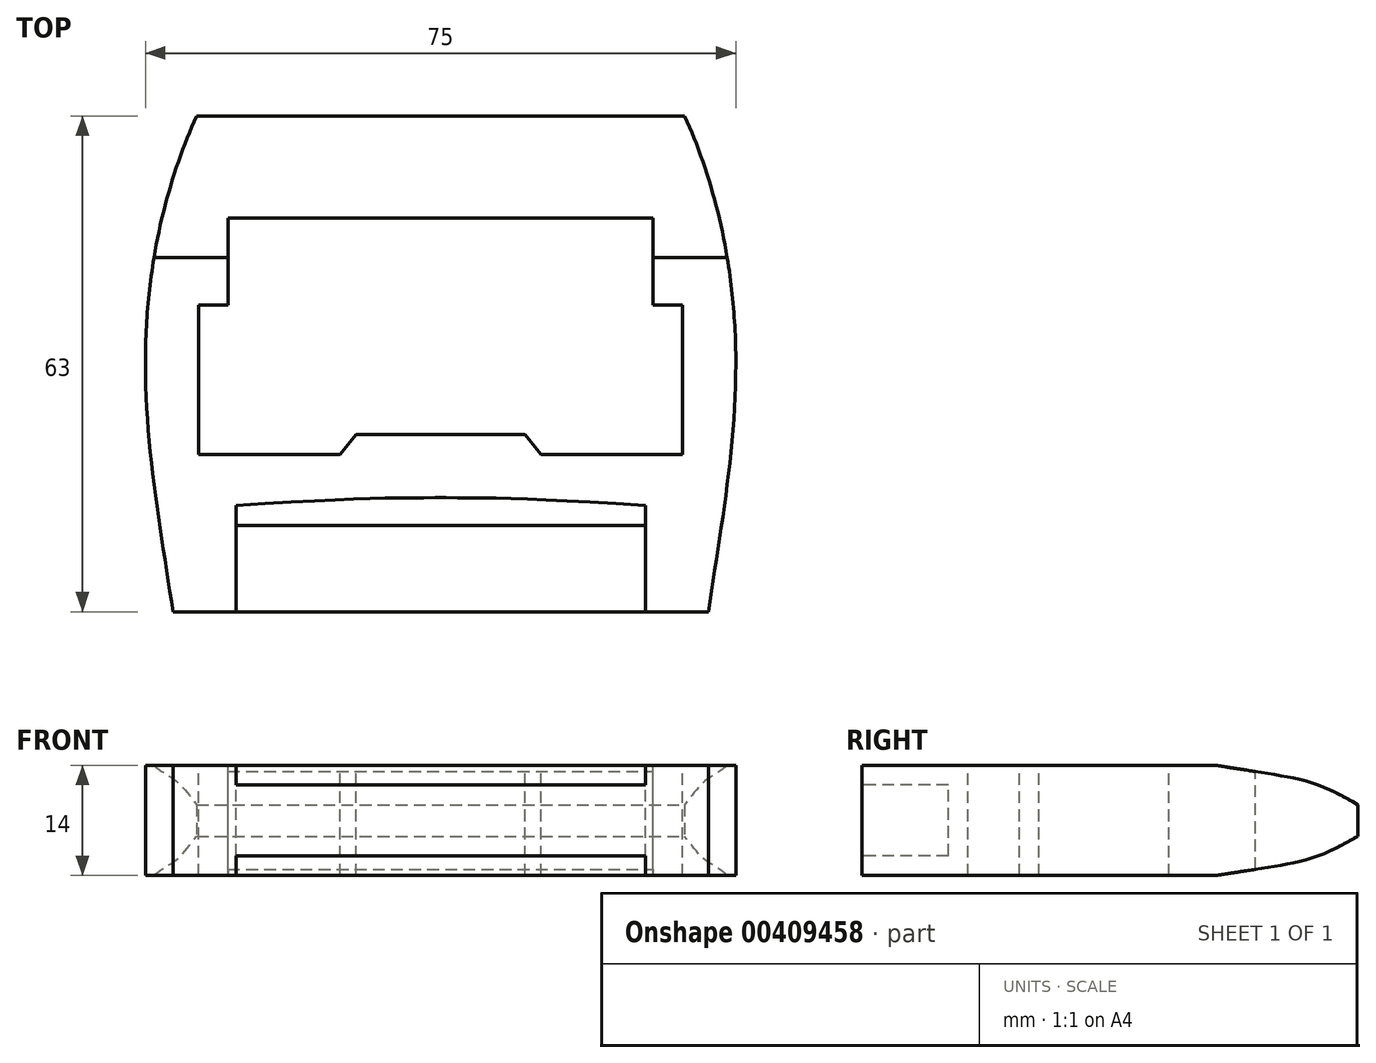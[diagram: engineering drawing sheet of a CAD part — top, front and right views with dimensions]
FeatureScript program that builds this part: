
annotation { "Feature Type Name" : "Feature", "Feature Type Description" : "" }
export const myFeature = defineFeature(function(context is Context, id is Id, definition is map)
    precondition{}
    {
        {
            var Q0;
            Q0=qCreatedBy(makeId("Top.planeOp"),FACE);
            var sketch = newSketch(context, id + "F0", { "sketchPlane" : qUnion([Q0])});
            skLineSegment(sketch, "E0.bottom", {"start": v(-37.5, 31.5) * mm, "end": v(37.5, 31.5) * mm});
            skLineSegment(sketch, "E0.top", {"start": v(-37.5, -31.5) * mm, "end": v(37.5, -31.5) * mm});
            skLineSegment(sketch, "E0.left", {"start": v(-37.5, 31.5) * mm, "end": v(-37.5, -31.5) * mm});
            skLineSegment(sketch, "E0.right", {"start": v(37.5, 31.5) * mm, "end": v(37.5, -31.5) * mm});
            skSolve(sketch);
        }
        {
            var Q0;
            Q0=makeQuery(id+"F0.imprint","IMPRINT",FACE,{"disambiguationData":[TD([[makeQuery(id+"F0.imprint","IMPRINT",EDGE,{"derivedFrom":sQuery(id+"F0.wireOp",EDGE,"E0.bottom")}),-1.0]])]});
            extrude(context, id + "F1", {"entities" : qUnion([Q0]), "depth" : 7 * mm});
        }
        {
            var Q0;
            Q0=makeQuery(id+"F1.opExtrude","CAP_FACE",FACE,{"disambiguationData":[OSD([sQuery(id+"F0.wireOp",EDGE,"E0.bottom"),sQuery(id+"F0.wireOp",EDGE,"E0.top"),sQuery(id+"F0.wireOp",EDGE,"E0.left"),sQuery(id+"F0.wireOp",EDGE,"E0.right")])],"isStart":false});
            var sketch = newSketch(context, id + "F2", { "sketchPlane" : qUnion([Q0])});
            skLineSegment(sketch, "E1", {"start": v(-27, 18.5) * mm, "end": v(27, 18.5) * mm});
            skLineSegment(sketch, "E2", {"start": v(27, 18.5) * mm, "end": v(27, 7.5) * mm});
            skLineSegment(sketch, "E3", {"start": v(27, 7.5) * mm, "end": v(30.75, 7.5) * mm});
            skLineSegment(sketch, "E4", {"start": v(30.75, 7.5) * mm, "end": v(30.75, -11.5) * mm});
            skLineSegment(sketch, "E5", {"start": v(30.75, -11.5) * mm, "end": v(12.75, -11.5) * mm});
            skLineSegment(sketch, "E6", {"start": v(-12.75, -11.5) * mm, "end": v(-30.75, -11.5) * mm});
            skLineSegment(sketch, "E7", {"start": v(-30.75, -11.5) * mm, "end": v(-30.75, 7.5) * mm});
            skLineSegment(sketch, "E8", {"start": v(-30.75, 7.5) * mm, "end": v(-27, 7.5) * mm});
            skLineSegment(sketch, "E9", {"start": v(-27, 7.5) * mm, "end": v(-27, 18.5) * mm});
            skLineSegment(sketch, "E10", {"start": v(-12.75, -11.5) * mm, "end": v(-10.75, -9) * mm});
            skLineSegment(sketch, "E11", {"start": v(-10.75, -9) * mm, "end": v(10.75, -9) * mm});
            skLineSegment(sketch, "E12", {"start": v(10.75, -9) * mm, "end": v(12.75, -11.5) * mm});
            skSolve(sketch);
        }
        {
            var Q0;
            Q0 = qSketchRegion(id + "F2", true);
            extrude(context, id + "F3", {"entities" : qUnion([Q0]), "operationType" : NewBodyOperationType.REMOVE, "oppositeDirection" : true, "depth" : 25 * mm});
        }
        {
            var Q0;
            Q0=makeQuery(id+"F1.opExtrude","CAP_FACE",FACE,{"disambiguationData":[OSD([sQuery(id+"F0.wireOp",EDGE,"E0.bottom"),sQuery(id+"F0.wireOp",EDGE,"E0.top"),sQuery(id+"F0.wireOp",EDGE,"E0.left"),sQuery(id+"F0.wireOp",EDGE,"E0.right")])],"isStart":false});
            var sketch = newSketch(context, id + "F4", { "sketchPlane" : qUnion([Q0])});
            skLineSegment(sketch, "E13", {"start": v(-26, -20.5) * mm, "end": v(26, -20.5) * mm});
            skLineSegment(sketch, "E14", {"start": v(26, -20.5) * mm, "end": v(26, -18) * mm});
            skLineSegment(sketch, "E15", {"start": v(-26, -20.5) * mm, "end": v(-26, -18) * mm});
            skFitSpline(sketch, "E16", {"points": [v(-26, -18) * mm, v(0, -17) * mm, v(26, -18) * mm], "startDerivative": vector(90, 6) * mm, "endDerivative": vector(90, -6) * mm});
            skSolve(sketch);
        }
        {
            var Q0;
            Q0 = qSketchRegion(id + "F4", true);
            extrude(context, id + "F5", {"entities" : qUnion([Q0]), "operationType" : NewBodyOperationType.REMOVE, "oppositeDirection" : true, "depth" : 25 * mm});
        }
        {
            var Q0;
            Q0=makeQuery(id+"F1.opExtrude","CAP_FACE",FACE,{"disambiguationData":[OSD([sQuery(id+"F0.wireOp",EDGE,"E0.bottom"),sQuery(id+"F0.wireOp",EDGE,"E0.top"),sQuery(id+"F0.wireOp",EDGE,"E0.left"),sQuery(id+"F0.wireOp",EDGE,"E0.right")])],"isStart":false});
            var sketch = newSketch(context, id + "F6", { "sketchPlane" : qUnion([Q0])});
            skLineSegment(sketch, "E17", {"start": v(-31, 31.5) * mm, "end": v(-31, 8.5) * mm});
            skLineSegment(sketch, "E18", {"start": v(-31, 8.5) * mm, "end": v(-35, 8.5) * mm});
            skLineSegment(sketch, "E19", {"start": v(-35, 8.5) * mm, "end": v(-35, -15.5) * mm});
            skLineSegment(sketch, "E20", {"start": v(-35, -15.5) * mm, "end": v(-26, -15.5) * mm});
            skLineSegment(sketch, "E21", {"start": v(-26, -15.5) * mm, "end": v(-26, -20.5) * mm});
            skLineSegment(sketch, "E22", {"start": v(26, -20.5) * mm, "end": v(26, -15.5) * mm});
            skLineSegment(sketch, "E23", {"start": v(26, -15.5) * mm, "end": v(35, -15.5) * mm});
            skLineSegment(sketch, "E24", {"start": v(35, -15.5) * mm, "end": v(35, 8.5) * mm});
            skLineSegment(sketch, "E25", {"start": v(35, 8.5) * mm, "end": v(31, 8.5) * mm});
            skLineSegment(sketch, "E26", {"start": v(31, 8.5) * mm, "end": v(31, 31.5) * mm});
            skLineSegment(sketch, "E27", {"start": v(37.5, 31.5) * mm, "end": v(31, 31.5) * mm});
            skLineSegment(sketch, "E28", {"start": v(-31, 31.5) * mm, "end": v(31, 31.5) * mm});
            skLineSegment(sketch, "E29", {"start": v(-26, -20.5) * mm, "end": v(26, -20.5) * mm});
            skPoint(sketch, "E30.orphan", {"position": v(-26, -31.5) * mm});
            skSolve(sketch);
        }
        {
            var Q0;
            Q0=makeQuery(id+"F1.opExtrude","CAP_FACE",FACE,{"disambiguationData":[OSD([sQuery(id+"F0.wireOp",EDGE,"E0.bottom"),sQuery(id+"F0.wireOp",EDGE,"E0.top"),sQuery(id+"F0.wireOp",EDGE,"E0.left"),sQuery(id+"F0.wireOp",EDGE,"E0.right")])],"isStart":false});
            var sketch = newSketch(context, id + "F7", { "sketchPlane" : qUnion([Q0])});
            skLineSegment(sketch, "E31", {"start": v(-26, -20.5) * mm, "end": v(-26, -31.5) * mm});
            skLineSegment(sketch, "E32", {"start": v(-26, -31.5) * mm, "end": v(26, -31.5) * mm});
            skLineSegment(sketch, "E33", {"start": v(26, -31.5) * mm, "end": v(26, -20.5) * mm});
            skLineSegment(sketch, "E34", {"start": v(26, -20.5) * mm, "end": v(-26, -20.5) * mm});
            skSolve(sketch);
        }
        {
            var Q0;
            Q0 = qSketchRegion(id + "F7", true);
            extrude(context, id + "F8", {"entities" : qUnion([Q0]), "operationType" : NewBodyOperationType.REMOVE, "oppositeDirection" : true, "depth" : 2.5 * mm});
        }
        {
            var Q0;
            Q0=makeQuery(id+"F1.opExtrude","SWEPT_FACE",FACE,{"disambiguationData":[OSD([sQuery(id+"F0.wireOp",EDGE,"E0.right")])]});
            var sketch = newSketch(context, id + "F9", { "sketchPlane" : qUnion([Q0])});
            skLineSegment(sketch, "E35", {"start": v(-31.5, 7) * mm, "end": v(13.5, 7) * mm});
            skFitSpline(sketch, "E36", {"points": [v(31.5, 2) * mm, v(23.7, 5.3) * mm, v(13.5, 7) * mm], "startDerivative": vector(-22.58, 13.06) * mm, "endDerivative": vector(-17.46, 2.94) * mm});
            skLineSegment(sketch, "E37", {"start": v(-31.5, 7) * mm, "end": v(-31.5, 11.1) * mm});
            skLineSegment(sketch, "E38", {"start": v(-31.5, 11.1) * mm, "end": v(31.5, 11.1) * mm});
            skLineSegment(sketch, "E39", {"start": v(31.5, 11.1) * mm, "end": v(31.5, 2) * mm});
            skSolve(sketch);
        }
        {
            var Q0;
            Q0 = qSketchRegion(id + "F9", true);
            extrude(context, id + "F10", {"entities" : qUnion([Q0]), "operationType" : NewBodyOperationType.REMOVE, "oppositeDirection" : true, "depth" : 80 * mm});
        }
        {
            var Q0;
            Q0=qCreatedBy(makeId("Top.planeOp"),FACE);
            var sketch = newSketch(context, id + "F11", { "sketchPlane" : qUnion([Q0])});
            skFitSpline(sketch, "E40", {"points": [v(-31, 31.5) * mm, v(-37.5, 0) * mm, v(-34, -31.5) * mm], "startDerivative": vector(-26.9, -59.78) * mm, "endDerivative": vector(9.03, -60.22) * mm});
            skFitSpline(sketch, "E41", {"points": [v(-31, 31.5) * mm, v(-31.98, 32.16) * mm], "startDerivative": vector(0.3, 1) * mm, "endDerivative": vector(0.65, -0.76) * mm});
            skLineSegment(sketch, "E42", {"start": v(-31, 31.5) * mm, "end": v(-43.32, 37.57) * mm});
            skLineSegment(sketch, "E43", {"start": v(-43.32, 37.57) * mm, "end": v(-41.83, -36.04) * mm});
            skLineSegment(sketch, "E44", {"start": v(-41.83, -36.04) * mm, "end": v(-34, -31.5) * mm});
            skFitSpline(sketch, "E45", {"points": [v(31, 31.5) * mm, v(37.5, 0) * mm, v(34, -31.5) * mm], "startDerivative": vector(26.9, -59.78) * mm, "endDerivative": vector(-9.03, -60.22) * mm});
            skLineSegment(sketch, "E46", {"start": v(31, 31.5) * mm, "end": v(39.7, 40.75) * mm});
            skLineSegment(sketch, "E47", {"start": v(39.7, 40.75) * mm, "end": v(45.62, -33.85) * mm});
            skLineSegment(sketch, "E48", {"start": v(45.62, -33.85) * mm, "end": v(34, -31.5) * mm});
            skSolve(sketch);
        }
        {
            var Q0;
            Q0 = qSketchRegion(id + "F11", true);
            extrude(context, id + "F12", {"entities" : qUnion([Q0]), "operationType" : NewBodyOperationType.REMOVE, "depth" : 25 * mm});
        }
        {
            var Q0;
            Q0=makeQuery(id+"F1.opExtrude","SWEPT_BODY",BODY,{"disambiguationData":[OSD([sQuery(id+"F0.wireOp",EDGE,"E0.bottom"),sQuery(id+"F0.wireOp",EDGE,"E0.top"),sQuery(id+"F0.wireOp",EDGE,"E0.left"),sQuery(id+"F0.wireOp",EDGE,"E0.right")])]});
            var Q1;
            Q1=qCreatedBy(makeId("Top.planeOp"),FACE);
            mirror(context, id + "F13", {"operationType" : NewBodyOperationType.ADD, "entities" : qUnion([Q0]), "mirrorPlane" : qUnion([Q1])});
        }
    });
